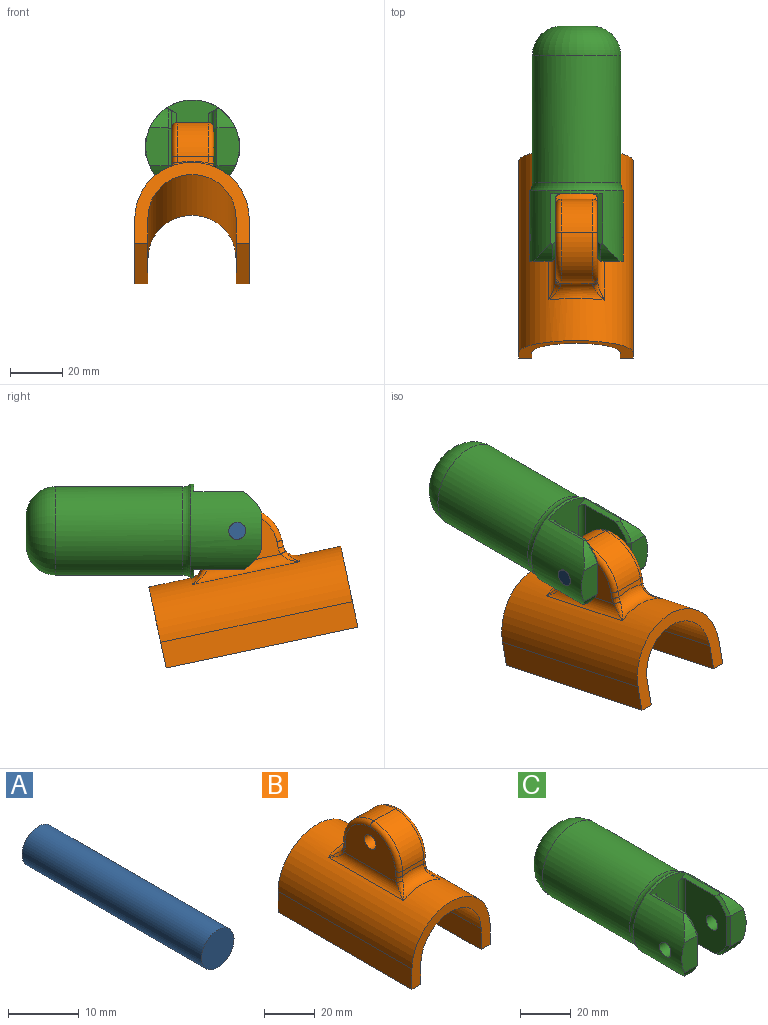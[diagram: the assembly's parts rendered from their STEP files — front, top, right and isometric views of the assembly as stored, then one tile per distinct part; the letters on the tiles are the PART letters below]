
ASSEMBLY  parts=3 mates=2
PART A: 3 faces, bbox 6.5x35.9x6.5 mm
  f0: cylinder r=3.25mm len=35.85mm, axis (0,1,0), area 732.1mm2, adj f1,f2
  f1: plane 6.5x6.5mm, normal (0,-1,0), area 33.2mm2, adj f0
  f2: plane 6.5x6.5mm, normal (0,1,0), area 33.2mm2, adj f0
PART B: 37 faces, bbox 43.7x75x56.2 mm
  f0: cylinder r=16.85mm len=75mm, axis (0,1,0), area 3970.2mm2, adj f2,f3,f31,f35
  f1: cylinder r=21.85mm len=75mm, axis (0,1,0), area 4192.5mm2, adj f2,f3,f8,f9,f10,f11,f32,f34
  f2: plane 43.7x31.66mm, normal (0,-1,0), area 395.8mm2, adj f0,f1,f31,f32,f33,f34,f35,f36
  f3: plane 43.7x31.66mm, normal (0,1,0), area 395.8mm2, adj f0,f1,f31,f32,f33,f34,f35,f36
  f4: plane 28.94x19.43mm, normal (-1,0,0), area 422.7mm2, adj f8,f14,f16,f17,f18,f19,f20,f21
  f5: plane 29.07x19.75mm, normal (1,0,0), area 431.7mm2, adj f9,f14,f24,f25,f26,f27,f28,f29
  f6: plane 12x2.57mm, normal (0,1,0), area 24.6mm2, adj f10,f12,f17,f25
  f7: plane 12x2.57mm, normal (0,-1,0), area 24.6mm2, adj f11,f13,f20,f28
  f8: cylinder r=5mm len=42mm, axis (0,1,0), area 185.5mm2, adj f1,f4,f15,f22
  f9: cylinder r=5mm len=42mm, axis (0,1,0), area 181.9mm2, adj f1,f5,f23,f30
  f10: torus R=26.85mm, axis (0,1,0), area 119.1mm2, adj f1,f6,f15,f16,f23,f24
  f11: torus R=26.85mm, axis (0,1,0), area 119.1mm2, adj f1,f7,f21,f22,f29,f30
  f12: cylinder r=16.42mm len=16.41mm, axis (1,0,0), area 304.4mm2, adj f6,f13,f18,f26
  f13: cylinder r=16.42mm len=16.41mm, axis (-1,0,0), area 304.4mm2, adj f7,f12,f19,f27
  f14: cylinder r=3.25mm len=16mm, axis (1,0,0), area 326.7mm2, adj f4,f5
  f15: bspline ~6.86x5.9mm, area 12.6mm2, adj f8,f10,f16
  f16: bspline ~5.66x2.86mm, area 6.7mm2, adj f4,f10,f15,f17
  f17: cylinder r=2mm len=2.44mm, axis (0,0,1), area 7.7mm2, adj f4,f6,f16,f18
  f18: torus R=14.42mm, axis (1,0,0), area 76.1mm2, adj f4,f12,f17,f19
  f19: torus R=14.42mm, axis (1,0,0), area 76.1mm2, adj f4,f13,f18,f20
  f20: cylinder r=2mm len=2.44mm, axis (0,0,-1), area 7.7mm2, adj f4,f7,f19,f21
  f21: bspline ~5.66x2.86mm, area 6.7mm2, adj f4,f11,f20,f22
  f22: bspline ~6.86x5.9mm, area 12.6mm2, adj f8,f11,f21
  f23: bspline ~6.82x5.89mm, area 12.3mm2, adj f9,f10,f24
  f24: bspline ~5.85x2.93mm, area 7.2mm2, adj f5,f10,f23,f25
  f25: cylinder r=2mm len=2.57mm, axis (0,0,-1), area 8.1mm2, adj f5,f6,f24,f26
  f26: torus R=14.42mm, axis (1,0,0), area 76.1mm2, adj f5,f12,f25,f27
  f27: torus R=14.42mm, axis (1,0,0), area 76.1mm2, adj f5,f13,f26,f28
  f28: cylinder r=2mm len=2.57mm, axis (0,0,1), area 8.1mm2, adj f5,f7,f27,f29
  f29: bspline ~5.85x2.93mm, area 7.2mm2, adj f5,f11,f28,f30
  f30: bspline ~6.82x5.89mm, area 12.3mm2, adj f9,f11,f29
  f31: plane 75x10mm, normal (1,0,0), area 750mm2, adj f0,f2,f3,f33
  f32: plane 75x10mm, normal (-1,0,0), area 750mm2, adj f1,f2,f3,f33
  f33: plane 75x5mm, normal (0,0,-1), area 375mm2, adj f2,f3,f31,f32
  f34: plane 75x10mm, normal (1,0,0), area 750mm2, adj f1,f2,f3,f36
  f35: plane 75x10mm, normal (-1,0,0), area 750mm2, adj f0,f2,f3,f36
  f36: plane 75x5mm, normal (0,0,-1), area 375mm2, adj f2,f3,f34,f35
PART C: 28 faces, bbox 39.8x90x39.8 mm
  f0: cylinder r=17.93mm len=35.85mm, axis (0,1,0), area 1757.8mm2, adj f1,f2,f5,f6,f7,f11,f12,f13
  f1: plane 14.48x8.6mm, normal (0,-1,0), area 117.3mm2, adj f0,f14,f15,f18
  f2: plane 14.48x8.6mm, normal (0,-1,0), area 117.3mm2, adj f0,f12,f13,f23
  f3: plane 27.77x22.6mm, normal (1,0,0), area 559.1mm2, adj f7,f16,f17,f18,f19,f20,f27
  f4: plane 27.77x22.6mm, normal (-1,0,0), area 559.1mm2, adj f6,f21,f22,f23,f24,f25,f26
  f5: plane 35.85x19.99mm, normal (0,-1,0), area 463.2mm2, adj f0,f16,f20,f21,f25,f26,f27
  f6: cylinder r=3.25mm len=9.8mm, axis (1,0,0), area 197.1mm2, adj f0,f4
  f7: cylinder r=3.25mm len=9.8mm, axis (1,0,0), area 197.1mm2, adj f0,f3
  f8: cylinder r=16.9mm len=48.62mm, axis (0,-1,0), area 5162.8mm2, adj f10,f11
  f9: plane 11.11x11.11mm, normal (0,1,0), area 96.9mm2, adj f10
  f10: torus R=5.55mm, axis (0,1,0), area 1430.9mm2, adj f8,f9
  f11: torus R=21.9mm, axis (0,-1,0), area 353.2mm2, adj f0,f8
  f12: cylinder r=17.26mm len=7.64mm, axis (1,0,0), area 43.6mm2, adj f0,f2,f24,f25
  f13: cylinder r=17.26mm len=7.64mm, axis (1,0,0), area 43.6mm2, adj f0,f2,f21,f22
  f14: cylinder r=17.26mm len=7.64mm, axis (1,0,0), area 43.6mm2, adj f0,f1,f19,f20
  f15: cylinder r=17.26mm len=7.64mm, axis (1,0,0), area 43.6mm2, adj f0,f1,f16,f17
  f16: plane 19.49x3.91mm, normal (0.47,0,0.88), area 41.1mm2, adj f0,f3,f5,f15,f17,f27
  f17: cone r=16.06mm half-angle=45deg, axis (-1,0,0), area 16.4mm2, adj f3,f15,f16,f18
  f18: plane 14.49x1.21mm, normal (0.71,-0.71,0), area 24.1mm2, adj f1,f3,f17,f19
  f19: cone r=16.06mm half-angle=45deg, axis (-1,0,0), area 16.4mm2, adj f3,f14,f18,f20
  f20: plane 19.49x3.91mm, normal (0.47,0,-0.88), area 41.1mm2, adj f0,f3,f5,f14,f19,f27
  f21: plane 19.49x3.91mm, normal (-0.47,0,0.88), area 41.1mm2, adj f0,f4,f5,f13,f22,f26
  f22: cone r=17.26mm half-angle=45deg, axis (1,0,0), area 16.4mm2, adj f4,f13,f21,f23
  f23: plane 14.49x1.21mm, normal (-0.71,-0.71,0), area 24.1mm2, adj f2,f4,f22,f24
  f24: cone r=17.26mm half-angle=45deg, axis (1,0,0), area 16.4mm2, adj f4,f12,f23,f25
  f25: plane 19.49x3.91mm, normal (-0.47,0,-0.88), area 41.1mm2, adj f0,f4,f5,f12,f24,f26
  f26: cylinder r=2mm len=27.77mm, axis (0,0,1), area 84.8mm2, adj f4,f5,f21,f25
  f27: cylinder r=2mm len=27.77mm, axis (0,0,-1), area 84.8mm2, adj f3,f5,f16,f20
PLACE A rot(axis=(-0.1,0.1,0.99),90.6deg) t=(10.76,-14.08,26.67)mm
PLACE B rot(axis=(-1,0,0),12deg) t=(10.76,-21.49,-8.2)mm
PLACE C rot(axis=(-0.85,0.52,0.08),0deg) t=(10.7,3.67,26.67)mm
MATE revolute C.f6 <-> A.f0  axis (1,0,0) through (28.69,-14.08,26.67)mm
MATE fastened B.f14 <-> A.f0  axis (1,0,0) through (10.76,-14.08,26.67)mm
